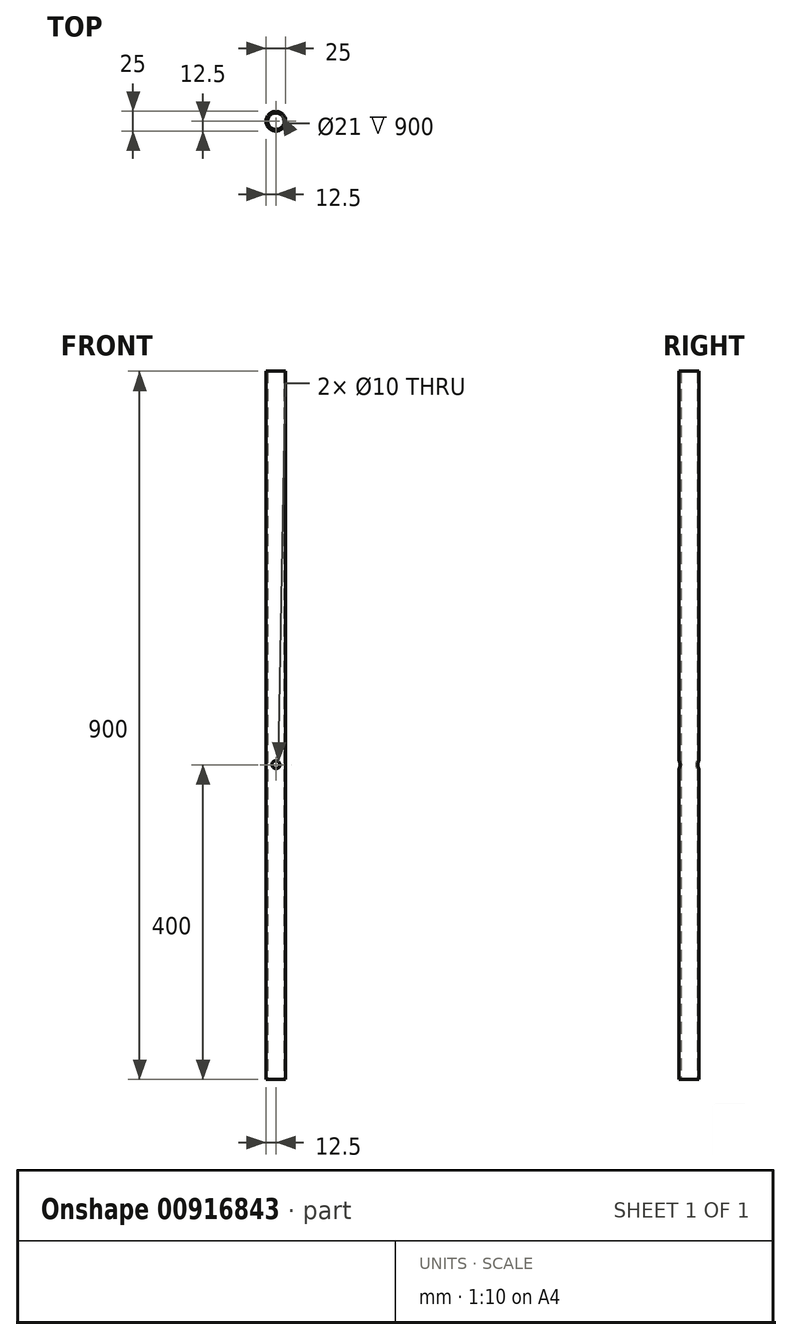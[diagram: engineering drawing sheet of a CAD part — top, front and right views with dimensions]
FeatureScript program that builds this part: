
annotation { "Feature Type Name" : "Feature", "Feature Type Description" : "" }
export const myFeature = defineFeature(function(context is Context, id is Id, definition is map)
    precondition{}
    {
        {
            var Q0;
            Q0=qCreatedBy(makeId("Top.planeOp"),FACE);
            var sketch = newSketch(context, id + "F0", { "sketchPlane" : qUnion([Q0])});
            skCircle(sketch, "E0", {"center": v(0, 0) * mm, "radius": 12.5 * mm});
            skCircle(sketch, "E1", {"center": v(0, 0) * mm, "radius": 10.5 * mm});
            skSolve(sketch);
        }
        {
            var Q0;
            Q0=qSketchRegion(id+"F0",true);
            extrude(context, id + "F1", {"entities" : qUnion([Q0]), "depth" : 500 * mm, "offsetDistance" : 25 * mm, "hasSecondDirection" : true, "secondDirectionOppositeDirection" : true, "secondDirectionDepth" : 400 * mm});
        }
        {
            var Q0;
            Q0=qCreatedBy(makeId("Front.planeOp"),FACE);
            var sketch = newSketch(context, id + "F2", { "sketchPlane" : qUnion([Q0])});
            skCircle(sketch, "E2", {"center": v(0, 0) * mm, "radius": 5 * mm});
            skSolve(sketch);
        }
        {
            var Q0;
            Q0=qSketchRegion(id+"F2",true);
            extrude(context, id + "F3", {"entities" : qUnion([Q0]), "operationType" : NewBodyOperationType.REMOVE, "oppositeDirection" : true, "depth" : 25 * mm, "offsetDistance" : 25 * mm, "hasSecondDirection" : true, "secondDirectionOppositeDirection" : false, "secondDirectionDepth" : 25 * mm});
        }
    });
